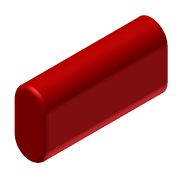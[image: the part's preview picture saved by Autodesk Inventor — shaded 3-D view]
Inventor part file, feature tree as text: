
AUTODESK INVENTOR PART (.ipt)
format: ipt  version: 2016 SP1 (Build 200210100, 210)  size: 86,016 bytes
history: native  units: mm (DEFAULTED — no unit token found)
features: extrude x1, fillet x1, sketch x1, reference x1
ambient origin geometry x8: Origin, YZ Plane, XZ Plane, XY Plane, X Axis, Y Axis, Z Axis, Center Point
bodies: Solid1 (feature_tree)
feature tree (4):
  extrude  "Extrusion1"  Depth=0.381mm
  fillet  "Fillet1"  [1 undecoded]
  sketch  "Sketch1"  dims[d0=12.7mm d1=0.0mm d2=0.381mm]
  reference  "Reference1"
note: 1 required parameter value undecoded (feature->parameter linkage not recoverable at this tier; creation-order binding heuristic only, values carry confidence <= 0.55)
